# Revit family: LBA_ALE_F16 100
name_source: partatom
category: Equipement spécialisé
revit_build: Autodesk Revit 2017 (Build: 20160225_1515(x64)
units: mm (PartAtom-declared; Revit-internal decimal feet)

## family parameters
Basée sur le plan de construction = Non
Cote de connecteur circulaire = Utiliser le diamètre
Couper avec des vides une fois chargée = Non
Partagée = Non
Point de calcul de pièce = Non
Toujours verticalement = Oui
Type d'élément = Normal

## types (1)
- LBA_B20
    Fabricant = AMCO Les Escamotables
    Matériau_borne = BORNE Fixe Rouge
    Matériau_massif = BORNE ANTHRACITE
    Modèle = ALE F16-100
    Type_massif = LBA_massif_sousterre_carré : Base
    URL = http://bornes-escamotables.com
    diamètre_borne = 160 mm  [stored 0.524934 ft]
    epaisseur_anneaux = 15 mm  [stored 0.0492126 ft]
    hauteur_borne = 980 mm  [stored 3.21522 ft]
    hauteur_massif = 650 mm  [stored 2.13255 ft]
    hauteur_sousface_batterie = 545 mm  [stored 1.78806 ft]
    l1_plaque = 218 mm  [stored 0.715223 ft]
    l2_plaque = 439 mm
    largeur_massif = 500 mm  [stored 1.64042 ft]
    longueur_massif = 500 mm  [stored 1.64042 ft]
    rayon_piston = 200 mm  [stored 0.656168 ft]
    rayon_vide = 80 mm  [stored 0.262467 ft]

note: [stored X ft] marks values corroborated as IEEE doubles in the binary element streams (Revit-internal decimal feet)
